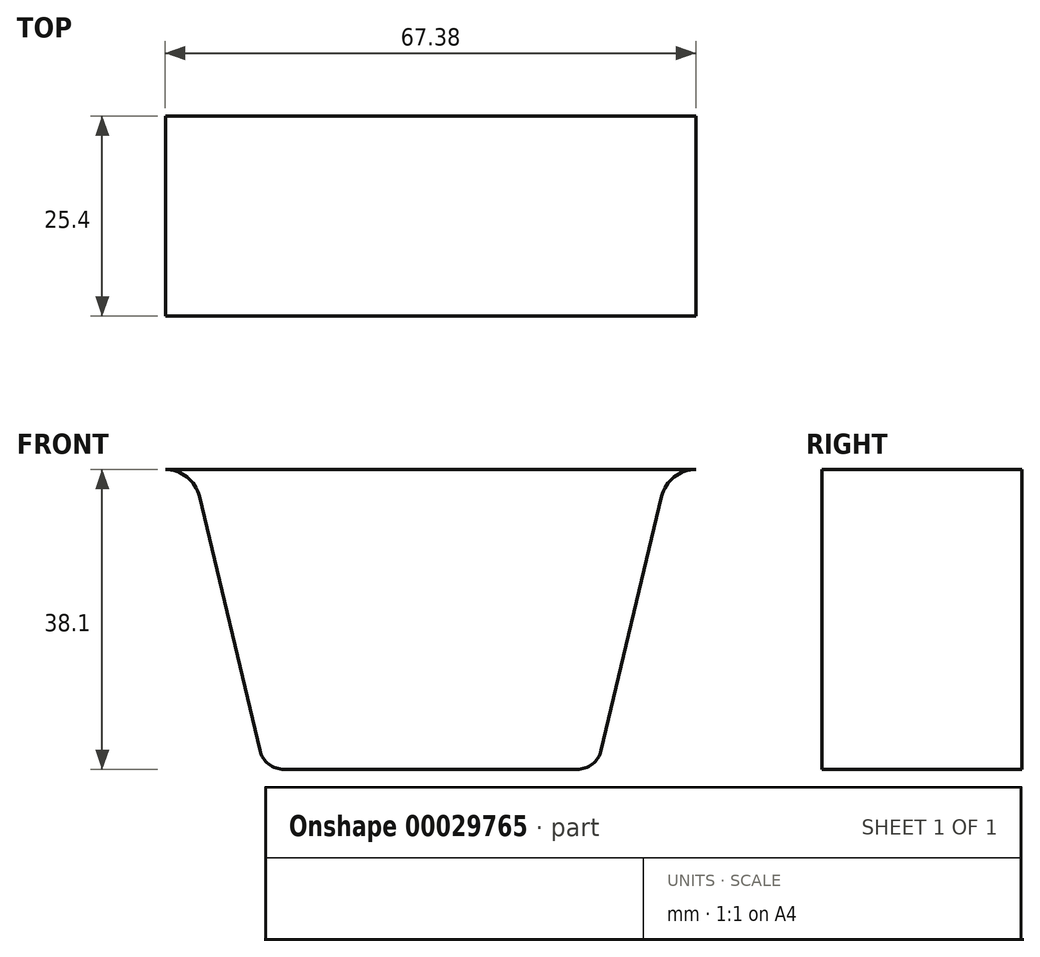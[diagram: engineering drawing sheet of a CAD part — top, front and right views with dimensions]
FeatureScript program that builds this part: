
annotation { "Feature Type Name" : "Feature", "Feature Type Description" : "" }
export const myFeature = defineFeature(function(context is Context, id is Id, definition is map)
    precondition{}
    {
        {
            var Q0;
            Q0=qCreatedBy(makeId("Front.planeOp"),FACE);
            var sketch = newSketch(context, id + "F0", { "sketchPlane" : qUnion([Q0])});
            skLineSegment(sketch, "E0", {"start": v(-446.13, -213.81) * mm, "end": v(-447.4, -213.81) * mm});
            skLineSegment(sketch, "E1", {"start": v(473.78, -227.57) * mm, "end": v(471.9, -212.26) * mm});
            skArc(sketch, "E2", {"start": v(471.9, -212.26) * mm, "mid": v(468.27, -209.05) * mm, "end": v(464.64, -212.26) * mm});
            skLineSegment(sketch, "E3", {"start": v(464.64, -212.26) * mm, "end": v(462.56, -229.18) * mm});
            skArc(sketch, "E4", {"start": v(462.56, -229.18) * mm, "mid": v(461.77, -230.68) * mm, "end": v(460.2, -231.28) * mm});
            skLineSegment(sketch, "E5", {"start": v(460.2, -231.28) * mm, "end": v(449.68, -231.28) * mm});
            skArc(sketch, "E6", {"start": v(449.68, -231.28) * mm, "mid": v(447.7, -230.6) * mm, "end": v(446.59, -228.84) * mm});
            skLineSegment(sketch, "E7", {"start": v(446.59, -228.84) * mm, "end": v(438.9, -196.6) * mm});
            skArc(sketch, "E8", {"start": v(438.9, -196.6) * mm, "mid": v(437.34, -194.13) * mm, "end": v(434.58, -193.18) * mm});
            skLineSegment(sketch, "E9", {"start": v(434.58, -193.18) * mm, "end": v(349.55, -193.18) * mm});
            skArc(sketch, "E10", {"start": v(349.55, -193.18) * mm, "mid": v(346.8, -194.13) * mm, "end": v(345.23, -196.6) * mm});
            skLineSegment(sketch, "E11", {"start": v(345.23, -196.6) * mm, "end": v(337.55, -228.84) * mm});
            skArc(sketch, "E12", {"start": v(337.55, -228.84) * mm, "mid": v(336.43, -230.6) * mm, "end": v(334.46, -231.28) * mm});
            skLineSegment(sketch, "E13", {"start": v(334.46, -231.28) * mm, "end": v(297.28, -231.28) * mm});
            skArc(sketch, "E14", {"start": v(297.28, -231.28) * mm, "mid": v(295.3, -230.6) * mm, "end": v(294.19, -228.84) * mm});
            skLineSegment(sketch, "E15", {"start": v(294.19, -228.84) * mm, "end": v(286.5, -196.6) * mm});
            skArc(sketch, "E16", {"start": v(286.5, -196.6) * mm, "mid": v(284.94, -194.13) * mm, "end": v(282.18, -193.18) * mm});
            skLineSegment(sketch, "E17", {"start": v(282.18, -193.18) * mm, "end": v(197.15, -193.18) * mm});
            skArc(sketch, "E18", {"start": v(197.15, -193.18) * mm, "mid": v(194.4, -194.13) * mm, "end": v(192.83, -196.6) * mm});
            skLineSegment(sketch, "E19", {"start": v(192.83, -196.6) * mm, "end": v(185.15, -228.84) * mm});
            skArc(sketch, "E20", {"start": v(185.15, -228.84) * mm, "mid": v(184.03, -230.6) * mm, "end": v(182.06, -231.28) * mm});
            skLineSegment(sketch, "E21", {"start": v(182.06, -231.28) * mm, "end": v(144.88, -231.28) * mm});
            skArc(sketch, "E22", {"start": v(144.88, -231.28) * mm, "mid": v(142.9, -230.6) * mm, "end": v(141.79, -228.84) * mm});
            skLineSegment(sketch, "E23", {"start": v(141.79, -228.84) * mm, "end": v(134.1, -196.6) * mm});
            skArc(sketch, "E24", {"start": v(134.1, -196.6) * mm, "mid": v(132.54, -194.13) * mm, "end": v(129.78, -193.18) * mm});
            skLineSegment(sketch, "E25", {"start": v(129.78, -193.18) * mm, "end": v(44.75, -193.18) * mm});
            skArc(sketch, "E26", {"start": v(44.75, -193.18) * mm, "mid": v(42, -194.13) * mm, "end": v(40.43, -196.6) * mm});
            skLineSegment(sketch, "E27", {"start": v(40.43, -196.6) * mm, "end": v(32.75, -228.84) * mm});
            skArc(sketch, "E28", {"start": v(32.75, -228.84) * mm, "mid": v(31.63, -230.6) * mm, "end": v(29.66, -231.28) * mm});
            skLineSegment(sketch, "E29", {"start": v(29.66, -231.28) * mm, "end": v(-7.52, -231.28) * mm});
            skArc(sketch, "E30", {"start": v(-7.52, -231.28) * mm, "mid": v(-9.5, -230.6) * mm, "end": v(-10.61, -228.84) * mm});
            skLineSegment(sketch, "E31", {"start": v(-10.61, -228.84) * mm, "end": v(-18.3, -196.6) * mm});
            skArc(sketch, "E32", {"start": v(-18.3, -196.6) * mm, "mid": v(-19.86, -194.13) * mm, "end": v(-22.62, -193.18) * mm});
            skLineSegment(sketch, "E33", {"start": v(-22.62, -193.18) * mm, "end": v(-107.65, -193.18) * mm});
            skArc(sketch, "E34", {"start": v(-107.65, -193.18) * mm, "mid": v(-110.4, -194.13) * mm, "end": v(-111.97, -196.6) * mm});
            skLineSegment(sketch, "E35", {"start": v(-111.97, -196.6) * mm, "end": v(-119.65, -228.84) * mm});
            skArc(sketch, "E36", {"start": v(-119.65, -228.84) * mm, "mid": v(-120.77, -230.6) * mm, "end": v(-122.74, -231.28) * mm});
            skLineSegment(sketch, "E37", {"start": v(-122.74, -231.28) * mm, "end": v(-159.92, -231.28) * mm});
            skArc(sketch, "E38", {"start": v(-159.92, -231.28) * mm, "mid": v(-161.9, -230.6) * mm, "end": v(-163.01, -228.84) * mm});
            skLineSegment(sketch, "E39", {"start": v(-163.01, -228.84) * mm, "end": v(-170.7, -196.6) * mm});
            skArc(sketch, "E40", {"start": v(-170.7, -196.6) * mm, "mid": v(-172.26, -194.13) * mm, "end": v(-175.02, -193.18) * mm});
            skLineSegment(sketch, "E41", {"start": v(-175.02, -193.18) * mm, "end": v(-260.05, -193.18) * mm});
            skArc(sketch, "E42", {"start": v(-260.05, -193.18) * mm, "mid": v(-262.8, -194.13) * mm, "end": v(-264.37, -196.6) * mm});
            skLineSegment(sketch, "E43", {"start": v(-264.37, -196.6) * mm, "end": v(-272.05, -228.84) * mm});
            skArc(sketch, "E44", {"start": v(-272.05, -228.84) * mm, "mid": v(-273.17, -230.6) * mm, "end": v(-275.14, -231.28) * mm});
            skLineSegment(sketch, "E45", {"start": v(-275.14, -231.28) * mm, "end": v(-312.32, -231.28) * mm});
            skArc(sketch, "E46", {"start": v(-312.32, -231.28) * mm, "mid": v(-314.3, -230.6) * mm, "end": v(-315.41, -228.84) * mm});
            skLineSegment(sketch, "E47", {"start": v(-315.41, -228.84) * mm, "end": v(-323.1, -196.6) * mm});
            skArc(sketch, "E48", {"start": v(-323.1, -196.6) * mm, "mid": v(-324.66, -194.13) * mm, "end": v(-327.42, -193.18) * mm});
            skLineSegment(sketch, "E49", {"start": v(-327.42, -193.18) * mm, "end": v(-412.45, -193.18) * mm});
            skArc(sketch, "E50", {"start": v(-412.45, -193.18) * mm, "mid": v(-415.2, -194.13) * mm, "end": v(-416.77, -196.6) * mm});
            skLineSegment(sketch, "E51", {"start": v(-416.77, -196.6) * mm, "end": v(-424.45, -228.84) * mm});
            skArc(sketch, "E52", {"start": v(-424.45, -228.84) * mm, "mid": v(-425.57, -230.6) * mm, "end": v(-427.54, -231.28) * mm});
            skLineSegment(sketch, "E53", {"start": v(-427.54, -231.28) * mm, "end": v(-442.96, -231.28) * mm});
            skArc(sketch, "E54", {"start": v(-442.96, -231.28) * mm, "mid": v(-445.2, -230.35) * mm, "end": v(-446.13, -228.1) * mm});
            skLineSegment(sketch, "E55", {"start": v(-446.13, -228.1) * mm, "end": v(-446.13, -213.81) * mm});
            skLineSegment(sketch, "E56", {"start": v(-447.4, -213.81) * mm, "end": v(-447.4, -228.1) * mm});
            skArc(sketch, "E57", {"start": v(-447.4, -228.1) * mm, "mid": v(-446.1, -231.24) * mm, "end": v(-442.96, -232.55) * mm});
            skLineSegment(sketch, "E58", {"start": v(-442.96, -232.55) * mm, "end": v(-427.54, -232.55) * mm});
            skArc(sketch, "E59", {"start": v(-427.54, -232.55) * mm, "mid": v(-424.79, -231.59) * mm, "end": v(-423.22, -229.13) * mm});
            skLineSegment(sketch, "E60", {"start": v(-423.22, -229.13) * mm, "end": v(-415.54, -196.88) * mm});
            skArc(sketch, "E61", {"start": v(-415.54, -196.88) * mm, "mid": v(-414.41, -195.13) * mm, "end": v(-412.45, -194.45) * mm});
            skLineSegment(sketch, "E62", {"start": v(-412.45, -194.45) * mm, "end": v(-327.42, -194.45) * mm});
            skArc(sketch, "E63", {"start": v(-327.42, -194.45) * mm, "mid": v(-325.45, -195.13) * mm, "end": v(-324.33, -196.88) * mm});
            skLineSegment(sketch, "E64", {"start": v(-324.33, -196.88) * mm, "end": v(-316.65, -229.13) * mm});
            skArc(sketch, "E65", {"start": v(-316.65, -229.13) * mm, "mid": v(-315.08, -231.59) * mm, "end": v(-312.32, -232.55) * mm});
            skLineSegment(sketch, "E66", {"start": v(-312.32, -232.55) * mm, "end": v(-275.14, -232.55) * mm});
            skArc(sketch, "E67", {"start": v(-275.14, -232.55) * mm, "mid": v(-272.39, -231.59) * mm, "end": v(-270.82, -229.13) * mm});
            skLineSegment(sketch, "E68", {"start": v(-270.82, -229.13) * mm, "end": v(-263.14, -196.88) * mm});
            skArc(sketch, "E69", {"start": v(-263.14, -196.88) * mm, "mid": v(-262.01, -195.13) * mm, "end": v(-260.05, -194.45) * mm});
            skLineSegment(sketch, "E70", {"start": v(-260.05, -194.45) * mm, "end": v(-175.02, -194.45) * mm});
            skArc(sketch, "E71", {"start": v(-175.02, -194.45) * mm, "mid": v(-173.05, -195.13) * mm, "end": v(-171.93, -196.88) * mm});
            skLineSegment(sketch, "E72", {"start": v(-171.93, -196.88) * mm, "end": v(-164.25, -229.13) * mm});
            skArc(sketch, "E73", {"start": v(-164.25, -229.13) * mm, "mid": v(-162.68, -231.59) * mm, "end": v(-159.92, -232.55) * mm});
            skLineSegment(sketch, "E74", {"start": v(-159.92, -232.55) * mm, "end": v(-122.74, -232.55) * mm});
            skArc(sketch, "E75", {"start": v(-122.74, -232.55) * mm, "mid": v(-119.99, -231.59) * mm, "end": v(-118.42, -229.13) * mm});
            skLineSegment(sketch, "E76", {"start": v(-118.42, -229.13) * mm, "end": v(-110.74, -196.88) * mm});
            skArc(sketch, "E77", {"start": v(-110.74, -196.88) * mm, "mid": v(-109.61, -195.13) * mm, "end": v(-107.65, -194.45) * mm});
            skLineSegment(sketch, "E78", {"start": v(-107.65, -194.45) * mm, "end": v(-22.62, -194.45) * mm});
            skArc(sketch, "E79", {"start": v(-22.62, -194.45) * mm, "mid": v(-20.65, -195.13) * mm, "end": v(-19.53, -196.88) * mm});
            skLineSegment(sketch, "E80", {"start": v(-19.53, -196.88) * mm, "end": v(-11.85, -229.13) * mm});
            skArc(sketch, "E81", {"start": v(-11.85, -229.13) * mm, "mid": v(-10.28, -231.59) * mm, "end": v(-7.52, -232.55) * mm});
            skLineSegment(sketch, "E82", {"start": v(-7.52, -232.55) * mm, "end": v(29.66, -232.55) * mm});
            skArc(sketch, "E83", {"start": v(29.66, -232.55) * mm, "mid": v(32.41, -231.59) * mm, "end": v(33.98, -229.13) * mm});
            skLineSegment(sketch, "E84", {"start": v(33.98, -229.13) * mm, "end": v(41.66, -196.88) * mm});
            skArc(sketch, "E85", {"start": v(41.66, -196.88) * mm, "mid": v(42.79, -195.13) * mm, "end": v(44.75, -194.45) * mm});
            skLineSegment(sketch, "E86", {"start": v(44.75, -194.45) * mm, "end": v(129.78, -194.45) * mm});
            skArc(sketch, "E87", {"start": v(129.78, -194.45) * mm, "mid": v(131.75, -195.13) * mm, "end": v(132.87, -196.88) * mm});
            skLineSegment(sketch, "E88", {"start": v(132.87, -196.88) * mm, "end": v(140.55, -229.13) * mm});
            skArc(sketch, "E89", {"start": v(140.55, -229.13) * mm, "mid": v(142.12, -231.59) * mm, "end": v(144.88, -232.55) * mm});
            skLineSegment(sketch, "E90", {"start": v(144.88, -232.55) * mm, "end": v(182.06, -232.55) * mm});
            skArc(sketch, "E91", {"start": v(182.06, -232.55) * mm, "mid": v(184.81, -231.59) * mm, "end": v(186.38, -229.13) * mm});
            skLineSegment(sketch, "E92", {"start": v(186.38, -229.13) * mm, "end": v(194.06, -196.88) * mm});
            skArc(sketch, "E93", {"start": v(194.06, -196.88) * mm, "mid": v(195.19, -195.13) * mm, "end": v(197.15, -194.45) * mm});
            skLineSegment(sketch, "E94", {"start": v(197.15, -194.45) * mm, "end": v(282.18, -194.45) * mm});
            skArc(sketch, "E95", {"start": v(282.18, -194.45) * mm, "mid": v(284.15, -195.13) * mm, "end": v(285.27, -196.88) * mm});
            skLineSegment(sketch, "E96", {"start": v(285.27, -196.88) * mm, "end": v(292.95, -229.13) * mm});
            skArc(sketch, "E97", {"start": v(292.95, -229.13) * mm, "mid": v(294.52, -231.59) * mm, "end": v(297.28, -232.55) * mm});
            skLineSegment(sketch, "E98", {"start": v(297.28, -232.55) * mm, "end": v(334.46, -232.55) * mm});
            skArc(sketch, "E99", {"start": v(334.46, -232.55) * mm, "mid": v(337.21, -231.59) * mm, "end": v(338.78, -229.13) * mm});
            skLineSegment(sketch, "E100", {"start": v(338.78, -229.13) * mm, "end": v(346.46, -196.88) * mm});
            skArc(sketch, "E101", {"start": v(346.46, -196.88) * mm, "mid": v(347.59, -195.13) * mm, "end": v(349.55, -194.45) * mm});
            skLineSegment(sketch, "E102", {"start": v(349.55, -194.45) * mm, "end": v(434.58, -194.45) * mm});
            skArc(sketch, "E103", {"start": v(434.58, -194.45) * mm, "mid": v(436.55, -195.13) * mm, "end": v(437.67, -196.88) * mm});
            skLineSegment(sketch, "E104", {"start": v(437.67, -196.88) * mm, "end": v(445.35, -229.13) * mm});
            skArc(sketch, "E105", {"start": v(445.35, -229.13) * mm, "mid": v(446.92, -231.59) * mm, "end": v(449.68, -232.55) * mm});
            skLineSegment(sketch, "E106", {"start": v(449.68, -232.55) * mm, "end": v(460.2, -232.55) * mm});
            skArc(sketch, "E107", {"start": v(460.2, -232.55) * mm, "mid": v(462.61, -231.63) * mm, "end": v(463.82, -229.33) * mm});
            skLineSegment(sketch, "E108", {"start": v(463.82, -229.33) * mm, "end": v(465.9, -212.42) * mm});
            skArc(sketch, "E109", {"start": v(465.9, -212.42) * mm, "mid": v(468.27, -210.32) * mm, "end": v(470.64, -212.42) * mm});
            skLineSegment(sketch, "E110", {"start": v(470.64, -212.42) * mm, "end": v(472.52, -227.72) * mm});
            skLineSegment(sketch, "E111", {"start": v(472.52, -227.72) * mm, "end": v(473.78, -227.57) * mm});
            skLineSegment(sketch, "E112", {"start": v(-460.59, -0.95) * mm, "end": v(-460.59, -15.24) * mm});
            skArc(sketch, "E113", {"start": v(-460.59, -15.24) * mm, "mid": v(-459.29, -18.38) * mm, "end": v(-456.14, -19.69) * mm});
            skLineSegment(sketch, "E114", {"start": v(-456.14, -19.69) * mm, "end": v(-440.73, -19.69) * mm});
            skArc(sketch, "E115", {"start": v(-440.73, -19.69) * mm, "mid": v(-437.97, -18.73) * mm, "end": v(-436.4, -16.27) * mm});
            skLineSegment(sketch, "E116", {"start": v(-436.4, -16.27) * mm, "end": v(-428.72, 15.98) * mm});
            skArc(sketch, "E117", {"start": v(-428.72, 15.98) * mm, "mid": v(-427.6, 17.73) * mm, "end": v(-425.63, 18.41) * mm});
            skLineSegment(sketch, "E118", {"start": v(-425.63, 18.41) * mm, "end": v(-340.6, 18.41) * mm});
            skArc(sketch, "E119", {"start": v(-340.6, 18.41) * mm, "mid": v(-338.64, 17.73) * mm, "end": v(-337.52, 15.98) * mm});
            skLineSegment(sketch, "E120", {"start": v(-337.52, 15.98) * mm, "end": v(-329.83, -16.27) * mm});
            skArc(sketch, "E121", {"start": v(-329.83, -16.27) * mm, "mid": v(-328.27, -18.73) * mm, "end": v(-325.51, -19.69) * mm});
            skLineSegment(sketch, "E122", {"start": v(-325.51, -19.69) * mm, "end": v(-288.33, -19.69) * mm});
            skArc(sketch, "E123", {"start": v(-288.33, -19.69) * mm, "mid": v(-285.57, -18.73) * mm, "end": v(-284, -16.27) * mm});
            skLineSegment(sketch, "E124", {"start": v(-284, -16.27) * mm, "end": v(-276.32, 15.98) * mm});
            skArc(sketch, "E125", {"start": v(-276.32, 15.98) * mm, "mid": v(-275.2, 17.73) * mm, "end": v(-273.23, 18.41) * mm});
            skLineSegment(sketch, "E126", {"start": v(-273.23, 18.41) * mm, "end": v(-188.2, 18.41) * mm});
            skArc(sketch, "E127", {"start": v(-188.2, 18.41) * mm, "mid": v(-186.24, 17.73) * mm, "end": v(-185.12, 15.98) * mm});
            skLineSegment(sketch, "E128", {"start": v(-185.12, 15.98) * mm, "end": v(-177.43, -16.27) * mm});
            skArc(sketch, "E129", {"start": v(-177.43, -16.27) * mm, "mid": v(-175.87, -18.73) * mm, "end": v(-173.11, -19.69) * mm});
            skLineSegment(sketch, "E130", {"start": v(-173.11, -19.69) * mm, "end": v(-135.93, -19.69) * mm});
            skArc(sketch, "E131", {"start": v(-135.93, -19.69) * mm, "mid": v(-133.17, -18.73) * mm, "end": v(-131.6, -16.27) * mm});
            skLineSegment(sketch, "E132", {"start": v(-131.6, -16.27) * mm, "end": v(-123.92, 15.98) * mm});
            skArc(sketch, "E133", {"start": v(-123.92, 15.98) * mm, "mid": v(-122.8, 17.73) * mm, "end": v(-120.83, 18.41) * mm});
            skLineSegment(sketch, "E134", {"start": v(-120.83, 18.41) * mm, "end": v(-35.8, 18.41) * mm});
            skArc(sketch, "E135", {"start": v(-35.8, 18.41) * mm, "mid": v(-33.84, 17.73) * mm, "end": v(-32.72, 15.98) * mm});
            skLineSegment(sketch, "E136", {"start": v(-32.72, 15.98) * mm, "end": v(-25.03, -16.27) * mm});
            skArc(sketch, "E137", {"start": v(-25.03, -16.27) * mm, "mid": v(-23.47, -18.73) * mm, "end": v(-20.71, -19.69) * mm});
            skLineSegment(sketch, "E138", {"start": v(-20.71, -19.69) * mm, "end": v(16.47, -19.69) * mm});
            skArc(sketch, "E139", {"start": v(16.47, -19.69) * mm, "mid": v(19.23, -18.73) * mm, "end": v(20.8, -16.27) * mm});
            skLineSegment(sketch, "E140", {"start": v(20.8, -16.27) * mm, "end": v(28.48, 15.98) * mm});
            skArc(sketch, "E141", {"start": v(28.48, 15.98) * mm, "mid": v(29.6, 17.73) * mm, "end": v(31.57, 18.41) * mm});
            skLineSegment(sketch, "E142", {"start": v(31.57, 18.41) * mm, "end": v(116.6, 18.41) * mm});
            skArc(sketch, "E143", {"start": v(116.6, 18.41) * mm, "mid": v(118.56, 17.73) * mm, "end": v(119.68, 15.98) * mm});
            skLineSegment(sketch, "E144", {"start": v(119.68, 15.98) * mm, "end": v(127.37, -16.27) * mm});
            skArc(sketch, "E145", {"start": v(127.37, -16.27) * mm, "mid": v(128.93, -18.73) * mm, "end": v(131.69, -19.69) * mm});
            skLineSegment(sketch, "E146", {"start": v(131.69, -19.69) * mm, "end": v(168.87, -19.69) * mm});
            skArc(sketch, "E147", {"start": v(168.87, -19.69) * mm, "mid": v(171.63, -18.73) * mm, "end": v(173.2, -16.27) * mm});
            skLineSegment(sketch, "E148", {"start": v(173.2, -16.27) * mm, "end": v(180.88, 15.98) * mm});
            skArc(sketch, "E149", {"start": v(180.88, 15.98) * mm, "mid": v(182, 17.73) * mm, "end": v(183.97, 18.41) * mm});
            skLineSegment(sketch, "E150", {"start": v(183.97, 18.41) * mm, "end": v(269, 18.41) * mm});
            skArc(sketch, "E151", {"start": v(269, 18.41) * mm, "mid": v(270.96, 17.73) * mm, "end": v(272.08, 15.98) * mm});
            skLineSegment(sketch, "E152", {"start": v(272.08, 15.98) * mm, "end": v(279.77, -16.27) * mm});
            skArc(sketch, "E153", {"start": v(279.77, -16.27) * mm, "mid": v(281.33, -18.73) * mm, "end": v(284.09, -19.69) * mm});
            skLineSegment(sketch, "E154", {"start": v(284.09, -19.69) * mm, "end": v(321.27, -19.69) * mm});
            skArc(sketch, "E155", {"start": v(321.27, -19.69) * mm, "mid": v(324.03, -18.73) * mm, "end": v(325.6, -16.27) * mm});
            skLineSegment(sketch, "E156", {"start": v(325.6, -16.27) * mm, "end": v(333.28, 15.98) * mm});
            skArc(sketch, "E157", {"start": v(333.28, 15.98) * mm, "mid": v(334.4, 17.73) * mm, "end": v(336.37, 18.41) * mm});
            skLineSegment(sketch, "E158", {"start": v(336.37, 18.41) * mm, "end": v(421.4, 18.41) * mm});
            skArc(sketch, "E159", {"start": v(421.4, 18.41) * mm, "mid": v(423.36, 17.73) * mm, "end": v(424.48, 15.98) * mm});
            skLineSegment(sketch, "E160", {"start": v(424.48, 15.98) * mm, "end": v(432.17, -16.27) * mm});
            skArc(sketch, "E161", {"start": v(432.17, -16.27) * mm, "mid": v(433.73, -18.73) * mm, "end": v(436.49, -19.69) * mm});
            skLineSegment(sketch, "E162", {"start": v(436.49, -19.69) * mm, "end": v(447, -19.69) * mm});
            skArc(sketch, "E163", {"start": v(447, -19.69) * mm, "mid": v(449.43, -18.77) * mm, "end": v(450.63, -16.47) * mm});
            skLineSegment(sketch, "E164", {"start": v(450.63, -16.47) * mm, "end": v(452.71, 0.44) * mm});
            skArc(sketch, "E165", {"start": v(452.71, 0.44) * mm, "mid": v(455.08, 2.54) * mm, "end": v(457.45, 0.44) * mm});
            skLineSegment(sketch, "E166", {"start": v(457.45, 0.44) * mm, "end": v(459.33, -14.86) * mm});
            skLineSegment(sketch, "E167", {"start": v(459.33, -14.86) * mm, "end": v(460.59, -14.7) * mm});
            skLineSegment(sketch, "E168", {"start": v(460.59, -14.7) * mm, "end": v(458.71, 0.6) * mm});
            skArc(sketch, "E169", {"start": v(458.71, 0.6) * mm, "mid": v(455.08, 3.81) * mm, "end": v(451.45, 0.6) * mm});
            skLineSegment(sketch, "E170", {"start": v(451.45, 0.6) * mm, "end": v(449.37, -16.32) * mm});
            skArc(sketch, "E171", {"start": v(449.37, -16.32) * mm, "mid": v(448.59, -17.82) * mm, "end": v(447, -18.41) * mm});
            skLineSegment(sketch, "E172", {"start": v(447, -18.41) * mm, "end": v(436.49, -18.41) * mm});
            skArc(sketch, "E173", {"start": v(436.49, -18.41) * mm, "mid": v(434.52, -17.73) * mm, "end": v(433.4, -15.98) * mm});
            skLineSegment(sketch, "E174", {"start": v(433.4, -15.98) * mm, "end": v(425.72, 16.27) * mm});
            skArc(sketch, "E175", {"start": v(425.72, 16.27) * mm, "mid": v(424.15, 18.73) * mm, "end": v(421.4, 19.69) * mm});
            skLineSegment(sketch, "E176", {"start": v(421.4, 19.69) * mm, "end": v(336.37, 19.69) * mm});
            skArc(sketch, "E177", {"start": v(336.37, 19.69) * mm, "mid": v(333.61, 18.73) * mm, "end": v(332.04, 16.27) * mm});
            skLineSegment(sketch, "E178", {"start": v(332.04, 16.27) * mm, "end": v(324.36, -15.98) * mm});
            skArc(sketch, "E179", {"start": v(324.36, -15.98) * mm, "mid": v(323.24, -17.73) * mm, "end": v(321.27, -18.41) * mm});
            skLineSegment(sketch, "E180", {"start": v(321.27, -18.41) * mm, "end": v(284.09, -18.41) * mm});
            skArc(sketch, "E181", {"start": v(284.09, -18.41) * mm, "mid": v(282.12, -17.73) * mm, "end": v(281, -15.98) * mm});
            skLineSegment(sketch, "E182", {"start": v(281, -15.98) * mm, "end": v(273.32, 16.27) * mm});
            skArc(sketch, "E183", {"start": v(273.32, 16.27) * mm, "mid": v(271.75, 18.73) * mm, "end": v(269, 19.69) * mm});
            skLineSegment(sketch, "E184", {"start": v(269, 19.69) * mm, "end": v(183.97, 19.69) * mm});
            skArc(sketch, "E185", {"start": v(183.97, 19.69) * mm, "mid": v(181.21, 18.73) * mm, "end": v(179.64, 16.27) * mm});
            skLineSegment(sketch, "E186", {"start": v(179.64, 16.27) * mm, "end": v(171.96, -15.98) * mm});
            skArc(sketch, "E187", {"start": v(171.96, -15.98) * mm, "mid": v(170.84, -17.73) * mm, "end": v(168.87, -18.41) * mm});
            skLineSegment(sketch, "E188", {"start": v(168.87, -18.41) * mm, "end": v(131.69, -18.41) * mm});
            skArc(sketch, "E189", {"start": v(131.69, -18.41) * mm, "mid": v(129.72, -17.73) * mm, "end": v(128.6, -15.98) * mm});
            skLineSegment(sketch, "E190", {"start": v(128.6, -15.98) * mm, "end": v(120.92, 16.27) * mm});
            skArc(sketch, "E191", {"start": v(120.92, 16.27) * mm, "mid": v(119.35, 18.73) * mm, "end": v(116.6, 19.69) * mm});
            skLineSegment(sketch, "E192", {"start": v(116.6, 19.69) * mm, "end": v(31.57, 19.69) * mm});
            skArc(sketch, "E193", {"start": v(31.57, 19.69) * mm, "mid": v(28.81, 18.73) * mm, "end": v(27.24, 16.27) * mm});
            skLineSegment(sketch, "E194", {"start": v(27.24, 16.27) * mm, "end": v(19.56, -15.98) * mm});
            skArc(sketch, "E195", {"start": v(19.56, -15.98) * mm, "mid": v(18.44, -17.73) * mm, "end": v(16.47, -18.41) * mm});
            skLineSegment(sketch, "E196", {"start": v(16.47, -18.41) * mm, "end": v(-20.71, -18.41) * mm});
            skArc(sketch, "E197", {"start": v(-20.71, -18.41) * mm, "mid": v(-22.68, -17.73) * mm, "end": v(-23.8, -15.98) * mm});
            skLineSegment(sketch, "E198", {"start": v(-23.8, -15.98) * mm, "end": v(-31.48, 16.27) * mm});
            skArc(sketch, "E199", {"start": v(-31.48, 16.27) * mm, "mid": v(-33.05, 18.73) * mm, "end": v(-35.8, 19.69) * mm});
            skLineSegment(sketch, "E200", {"start": v(-35.8, 19.69) * mm, "end": v(-120.83, 19.69) * mm});
            skArc(sketch, "E201", {"start": v(-120.83, 19.69) * mm, "mid": v(-123.59, 18.73) * mm, "end": v(-125.16, 16.27) * mm});
            skLineSegment(sketch, "E202", {"start": v(-125.16, 16.27) * mm, "end": v(-132.84, -15.98) * mm});
            skArc(sketch, "E203", {"start": v(-132.84, -15.98) * mm, "mid": v(-133.96, -17.73) * mm, "end": v(-135.93, -18.41) * mm});
            skLineSegment(sketch, "E204", {"start": v(-135.93, -18.41) * mm, "end": v(-173.11, -18.41) * mm});
            skArc(sketch, "E205", {"start": v(-173.11, -18.41) * mm, "mid": v(-175.08, -17.73) * mm, "end": v(-176.2, -15.98) * mm});
            skLineSegment(sketch, "E206", {"start": v(-176.2, -15.98) * mm, "end": v(-183.88, 16.27) * mm});
            skArc(sketch, "E207", {"start": v(-183.88, 16.27) * mm, "mid": v(-185.45, 18.73) * mm, "end": v(-188.2, 19.69) * mm});
            skLineSegment(sketch, "E208", {"start": v(-188.2, 19.69) * mm, "end": v(-273.23, 19.69) * mm});
            skArc(sketch, "E209", {"start": v(-273.23, 19.69) * mm, "mid": v(-275.99, 18.73) * mm, "end": v(-277.56, 16.27) * mm});
            skLineSegment(sketch, "E210", {"start": v(-277.56, 16.27) * mm, "end": v(-285.24, -15.98) * mm});
            skArc(sketch, "E211", {"start": v(-285.24, -15.98) * mm, "mid": v(-286.36, -17.73) * mm, "end": v(-288.33, -18.41) * mm});
            skLineSegment(sketch, "E212", {"start": v(-288.33, -18.41) * mm, "end": v(-325.51, -18.41) * mm});
            skArc(sketch, "E213", {"start": v(-325.51, -18.41) * mm, "mid": v(-327.48, -17.73) * mm, "end": v(-328.6, -15.98) * mm});
            skLineSegment(sketch, "E214", {"start": v(-328.6, -15.98) * mm, "end": v(-336.28, 16.27) * mm});
            skArc(sketch, "E215", {"start": v(-336.28, 16.27) * mm, "mid": v(-337.85, 18.73) * mm, "end": v(-340.6, 19.69) * mm});
            skLineSegment(sketch, "E216", {"start": v(-340.6, 19.69) * mm, "end": v(-425.63, 19.69) * mm});
            skArc(sketch, "E217", {"start": v(-425.63, 19.69) * mm, "mid": v(-428.39, 18.73) * mm, "end": v(-429.96, 16.27) * mm});
            skLineSegment(sketch, "E218", {"start": v(-429.96, 16.27) * mm, "end": v(-437.64, -15.98) * mm});
            skArc(sketch, "E219", {"start": v(-437.64, -15.98) * mm, "mid": v(-438.76, -17.73) * mm, "end": v(-440.73, -18.41) * mm});
            skLineSegment(sketch, "E220", {"start": v(-440.73, -18.41) * mm, "end": v(-456.14, -18.41) * mm});
            skArc(sketch, "E221", {"start": v(-456.14, -18.41) * mm, "mid": v(-458.39, -17.49) * mm, "end": v(-459.32, -15.24) * mm});
            skLineSegment(sketch, "E222", {"start": v(-459.32, -15.24) * mm, "end": v(-459.32, -0.95) * mm});
            skLineSegment(sketch, "E223", {"start": v(-459.32, -0.95) * mm, "end": v(-460.59, -0.95) * mm});
            skSolve(sketch);
        }
        {
            var Q0;
            Q0=qCreatedBy(makeId("Front.planeOp"),FACE);
            var sketch = newSketch(context, id + "F1", { "sketchPlane" : qUnion([Q0])});
            skLineSegment(sketch, "E224", {"start": v(-35.8, 19.69) * mm, "end": v(31.57, 19.69) * mm});
            skLineSegment(sketch, "E225", {"start": v(16.47, -18.41) * mm, "end": v(-20.71, -18.42) * mm});
            skArc(sketch, "E226", {"start": v(-31.48, 16.27) * mm, "mid": v(-33.05, 18.73) * mm, "end": v(-35.8, 19.69) * mm});
            skArc(sketch, "E227", {"start": v(31.57, 19.69) * mm, "mid": v(28.81, 18.73) * mm, "end": v(27.24, 16.27) * mm});
            skArc(sketch, "E228", {"start": v(-23.8, -15.98) * mm, "mid": v(-22.68, -17.73) * mm, "end": v(-20.71, -18.41) * mm});
            skArc(sketch, "E229", {"start": v(16.47, -18.41) * mm, "mid": v(18.44, -17.73) * mm, "end": v(19.56, -15.98) * mm});
            skLineSegment(sketch, "E230", {"start": v(-31.48, 16.27) * mm, "end": v(-23.8, -15.98) * mm});
            skLineSegment(sketch, "E231", {"start": v(19.56, -15.98) * mm, "end": v(27.24, 16.27) * mm});
            skSolve(sketch);
        }
        {
            var Q0;
            Q0=makeQuery(id+"F1.imprint","IMPRINT",FACE,{"disambiguationData":[TD([[makeQuery(id+"F1.imprint","IMPRINT",EDGE,{"derivedFrom":sQuery(id+"F1.wireOp",EDGE,"E224")}),-1.0]])]});
            extrude(context, id + "F2", {"entities" : qUnion([Q0]), "depth" : 25.4 * mm});
        }
    });
